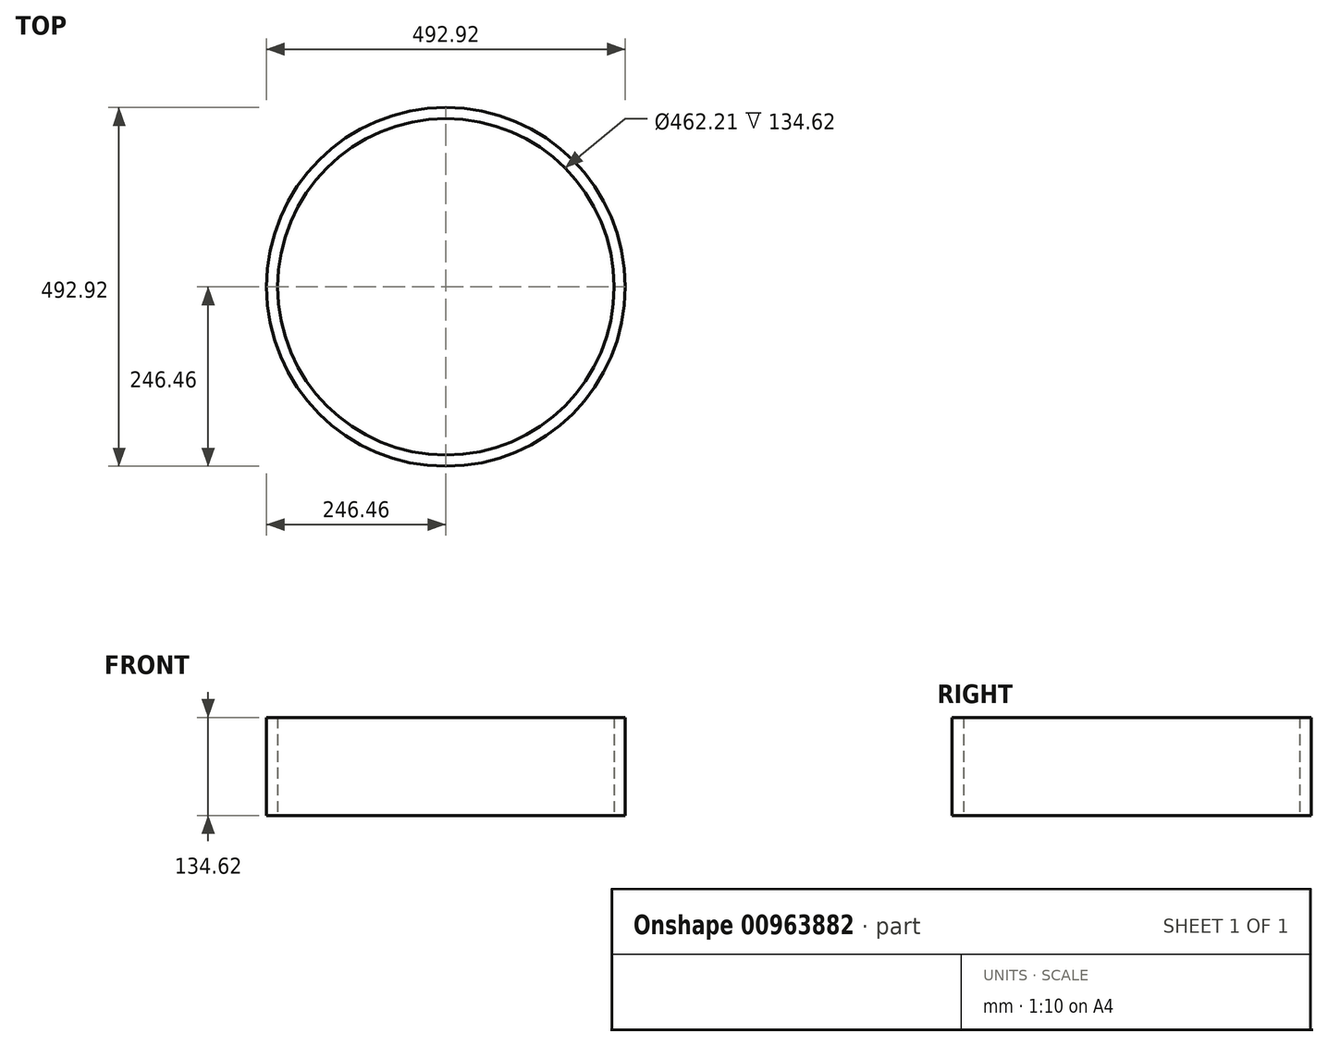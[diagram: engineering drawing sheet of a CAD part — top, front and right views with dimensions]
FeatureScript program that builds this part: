
annotation { "Feature Type Name" : "Feature", "Feature Type Description" : "" }
export const myFeature = defineFeature(function(context is Context, id is Id, definition is map)
    precondition{}
    {
        {
            var Q0;
            Q0=qCreatedBy(makeId("Top.planeOp"),FACE);
            var sketch = newSketch(context, id + "F0", { "sketchPlane" : qUnion([Q0])});
            skCircle(sketch, "E0", {"center": v(0, 0) * mm, "radius": 231.1 * mm});
            skCircle(sketch, "E1", {"center": v(0, 0) * mm, "radius": 246.46 * mm});
            skSolve(sketch);
        }
        {
            var Q0;
            Q0=makeQuery(id+"F0.imprint","IMPRINT",FACE,{"disambiguationData":[TD([[makeQuery(id+"F0.imprint","IMPRINT",EDGE,{"derivedFrom":sQuery(id+"F0.wireOp",EDGE,"E0")}),-1.0]])]});
            var Q1;
            Q1=sQuery(id+"F0.wireOp",EDGE,"E1");
            var Q2;
            Q2=sQuery(id+"F0.wireOp",EDGE,"E0");
            extrude(context, id + "F1", {"entities" : qUnion([Q0]), "surfaceOperationType" : NewSurfaceOperationType.ADD, "surfaceEntities" : qUnion([Q1, Q2]), "depth" : 134.62 * mm, "offsetDistance" : 25.4 * mm, "symmetric" : true});
        }
    });
